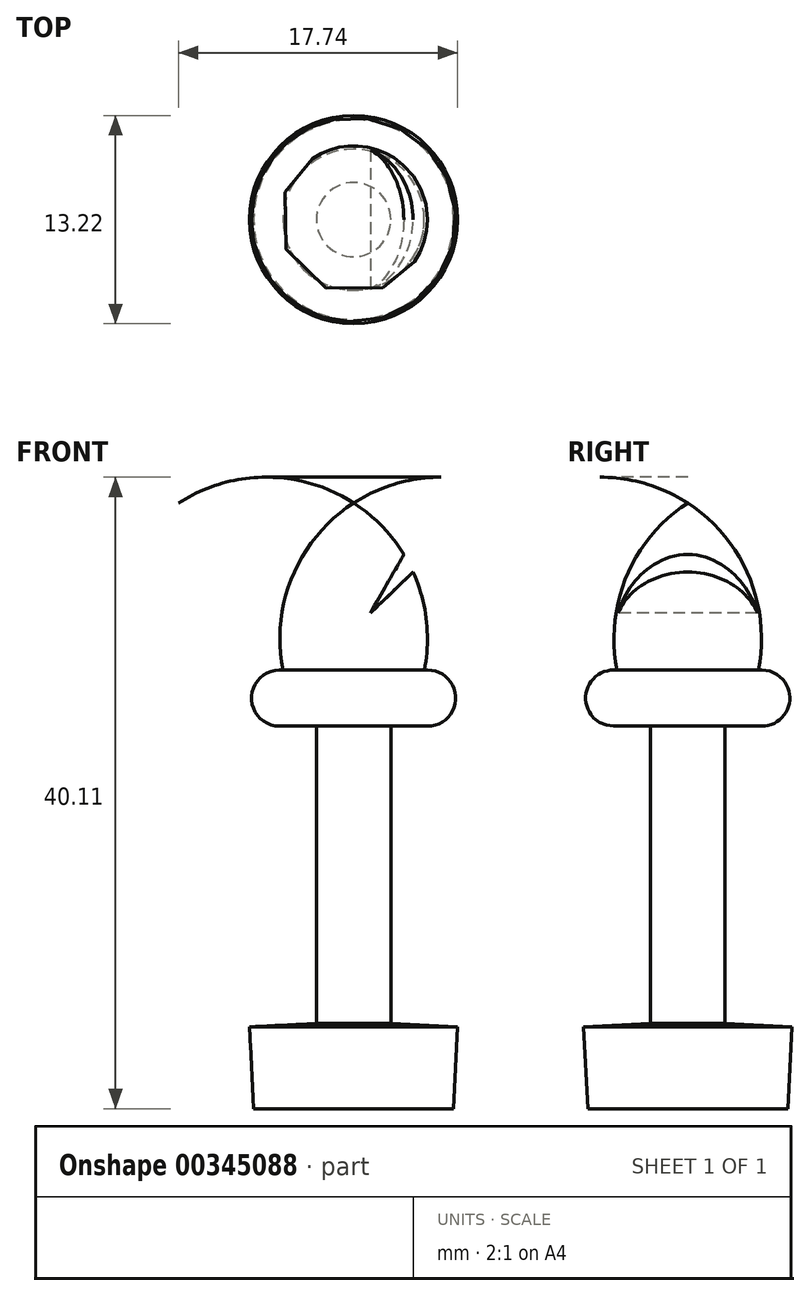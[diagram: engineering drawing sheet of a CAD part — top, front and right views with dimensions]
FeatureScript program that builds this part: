
annotation { "Feature Type Name" : "Feature", "Feature Type Description" : "" }
export const myFeature = defineFeature(function(context is Context, id is Id, definition is map)
    precondition{}
    {
        {
            var Q0;
            Q0=qCreatedBy(makeId("Front.planeOp"),FACE);
            var sketch = newSketch(context, id + "F0", { "sketchPlane" : qUnion([Q0])});
            skArc(sketch, "E0", {"start": v(4.48, 24.3) * mm, "mid": v(6.49, 26.08) * mm, "end": v(4.48, 27.85) * mm});
            skPoint(sketch, "E1.end.orphan", {"position": v(0, 38.47) * mm});
            skLineSegment(sketch, "E2", {"start": v(0, 0) * mm, "end": v(0, 38.47) * mm});
            skArc(sketch, "E3", {"start": v(4.48, 27.85) * mm, "mid": v(3.88, 33.85) * mm, "end": v(0, 38.47) * mm});
            skLineSegment(sketch, "E4", {"start": v(2.36, 24.3) * mm, "end": v(4.48, 24.3) * mm});
            skPoint(sketch, "E5.start.orphan", {"position": v(8.9, 3.05) * mm});
            skPoint(sketch, "E6.orphan", {"position": v(8.9, 0) * mm});
            skPoint(sketch, "E7.end.orphan", {"position": v(4.45, 0) * mm});
            skLineSegment(sketch, "E8", {"start": v(0, 0) * mm, "end": v(6.35, 0) * mm});
            skLineSegment(sketch, "E9", {"start": v(2.36, 24.3) * mm, "end": v(2.36, 5.4) * mm});
            skPoint(sketch, "E10.end.orphan", {"position": v(6.6, 3.05) * mm});
            skPoint(sketch, "E11.end.orphan", {"position": v(4.48, 3.05) * mm});
            skLineSegment(sketch, "E12", {"start": v(6.35, 0) * mm, "end": v(6.6, 5.2) * mm});
            skLineSegment(sketch, "E13", {"start": v(6.6, 5.2) * mm, "end": v(2.36, 5.4) * mm});
            skPoint(sketch, "E14.orphan", {"position": v(2.36, 3.05) * mm});
            skPoint(sketch, "E15.orphan", {"position": v(6.84, 38.47) * mm});
            skPoint(sketch, "E16.orphan", {"position": v(4.01, 38.47) * mm});
            skSolve(sketch);
        }
        {
            var Q0;
            Q0 = qSketchRegion(id + "F0", true);
            var Q1;
            Q1=sQuery(id+"F0.wireOp",EDGE,"E2");
            revolve(context, id + "F1", {"entities" : qUnion([Q0]), "axis" : qUnion([Q1]), "revolveType" : RevolveType.FULL});
        }
        {
            var Q0;
            Q0=qCreatedBy(makeId("Front.planeOp"),FACE);
            var sketch = newSketch(context, id + "F2", { "sketchPlane" : qUnion([Q0])});
            skLineSegment(sketch, "E17", {"start": v(5.9, 36.11) * mm, "end": v(4.25, 37.05) * mm});
            skLineSegment(sketch, "E18", {"start": v(4.25, 37.05) * mm, "end": v(1.07, 31.49) * mm});
            skLineSegment(sketch, "E19", {"start": v(1.07, 31.49) * mm, "end": v(5.9, 36.11) * mm});
            skSolve(sketch);
        }
        {
            var Q0;
            Q0 = qSketchRegion(id + "F2", true);
            extrude(context, id + "F3", {"entities" : qUnion([Q0]), "operationType" : NewBodyOperationType.REMOVE, "oppositeDirection" : true, "depth" : 25.4 * mm});
        }
        {
            var Q0;
            Q0 = qSketchRegion(id + "F2", true);
            extrude(context, id + "F4", {"entities" : qUnion([Q0]), "operationType" : NewBodyOperationType.REMOVE, "depth" : 77.72 * mm});
        }
    });
